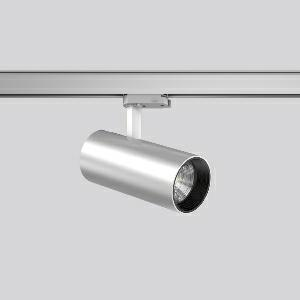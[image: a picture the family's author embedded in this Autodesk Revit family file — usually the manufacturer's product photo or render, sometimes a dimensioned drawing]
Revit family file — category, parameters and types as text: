
# Revit family: deecos_s_mini_742207_004_3_26a8
name_source: partatom
category: Lighting Fixtures
units: mm (PartAtom-declared; Revit-internal decimal feet)

## family parameters
Cut with Voids When Loaded = No
Host = Face
Light Source = No
Part Type = Normal
Room Calculation Point = No
Round Connector Dimension = Use Diameter
Shared = No

## types (1)
- DEECOS S mini (1 x LED Modul 935, 3050 lm, 3500)
    Apparent Load = 29 VA
    Approval mark = CE
    CIE Flux Codes = 96 100 100 100 100
    Color Rendering = 92
    Color Temperature = 3500
    Default Elevation = 1800 mm
    Description = Series: DEECOS S mini
LED surface-mounted projector in modern design with no visible cooling ribs. Housing: die-cast aluminium, powder-coated. Rotation range: 356°. Swivel range: 90°. Black plastic ring and recessed LED to prevent glare from the side. Optical assembly with lens made of plastic (polycarbonate) for the best homogeneous light distribution - can be changed without tools. Best colour rendering index Ra>90. With multi adaptor for 3-circuit tracks 230 V. Suitable for Track on ceiling, Wall track. High quality converter without flickering and stroboscopic effect. The following accessories can be mounted without use of tools: interchangeable lenses, decorative glasses, honeycomb louvre, clear and frosted diffusers, white interchangeable plastic ring. 
Colour: silver
Diameter: 87 mm
Height: 214 mm
Lamp: LED
Socket: without socket
Colour temperature: 3500K
Colour rendering index (CRI): 92
System power: 29 W
Rated luminous flux: 3050 lm
Luminous efficiency: 105 lm/W
Control gear: Regulated power supply
Protection class: I
Type of protection: IP 20
    Height = 214 mm
    Lamp = 1 x LED Modul 935
    Lamp Light Flux = 3050 lm
    Lamp count = 1
    Length = 87 mm
    Lifetime = 50000 h
    Luminous efficacy = 105 lm/W
    Manufacturer = RZB
    ModVariant = No
    Model = 742207.004.3
    Mounting Place = Ceiling
    Mounting Type = Rail mounted
    Number of Poles = 1
    OnlyDefault = Yes
    Power Factor = 1
    Product Name = DEECOS S mini
    Product group = Track mounted projectors
    ProductGroupID = 301
    Protection Class = Protection class I
    Protection Degree = IP 20
    RLX_Detail_Level = 1
    RLX_Emergency_Light_Flux = 0 lm
    RLX_Emergency_Type = 0
    RLX_Emergency_Type_DB = No
    RlxData = <blob elided: 37185 chars, md5=b099e67b>
    Socket = socket
    Standby Power = 0 W
    System Light Flux = 3050 lm
    System Power = 29 W
    Type Comments = Product without accessories
    Type Image = 741930.004.jpg
    URL = http://relux.com
    VarID = ---
    Voltage = 230 V
    Voltage Range = 220-240 V
    Weight = 0.00 kg
    Width = 0 mm  [stored 0 ft]

note: [stored X ft] marks values corroborated as IEEE doubles in the binary element streams (Revit-internal decimal feet)

## geometry (parser evidence)
native form markers: Blend x4, Sweep x11
no freeform markers — native parametric forms only
